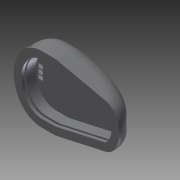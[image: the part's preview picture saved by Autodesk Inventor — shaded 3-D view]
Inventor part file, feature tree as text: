
AUTODESK INVENTOR PART (.ipt)
format: ipt  version: 2015 (Build 190159000, 159)  size: 722,432 bytes
history: native  units: mm
features: extrude x8, sketch x8, fillet x6, projected_geometry x5, plane x1
ambient origin geometry x8: Origin, YZ Plane, XZ Plane, XY Plane, X Axis, Y Axis, Z Axis, Center Point
bodies: Solid1 (feature_tree)
feature tree (28):
  extrude  "Extrusion1"  Depth=60.0mm
  fillet  "Fillet1"  Radius=20.0mm
  extrude  "Extrusion2"  Depth=30.0mm TaperAngle=0.0deg
  fillet  "Fillet6"  Radius=15.0mm
  fillet  "Fillet7"  Radius=110.0mm
  extrude  "Extrusion6"  Depth=60.0mm
  extrude  "Extrusion7"  Depth=5.0mm
  plane  "Work Plane2"
  extrude  "Extrusion8"  Depth=16.0mm
  fillet  "Fillet8"  Radius=8.0mm
  fillet  "Fillet9"  Radius=15.0mm
  extrude  "Extrusion9"  Depth=20.0mm
  extrude  "Extrusion10"  Depth=5.0mm TaperAngle=0.0deg
  fillet  "Fillet10"  Radius=15.5mm
  extrude  "Extrusion12"  Depth=1.0mm
  sketch  "Sketch1"  dims[d0=80.0mm d1=60.0mm d2=20.0mm]
  sketch  "Sketch2"  dims[d3=20.0mm d4=30.0mm d5=0.0mm d6=15.0mm d9=110.0mm]
  sketch  "Sketch6"  dims[d12=50.0mm d13=60.0mm]
  projected_geometry  "Projected Loop3"
  sketch  "Sketch8"  dims[d14=69.25mm d15=0.0mm d33=5.0mm]
  sketch  "Sketch9"  dims[d34=27.0mm d35=16.0mm d36=8.0mm d37=15.0mm d38=0.0mm]
  projected_geometry  "Projected Loop4"
  sketch  "Sketch10"  dims[d40=15.0mm d41=20.0mm]
  projected_geometry  "Projected Loop5"
  sketch  "Sketch11"  dims[d42=8.0mm d43=5.0mm d44=0.0mm d49=15.5mm d50=0.0mm]
  projected_geometry  "Projected Loop6"
  sketch  "Sketch13"  dims[d51=4.0mm d52=1.0mm d53=4.0mm d54=1.0mm d55=4.0mm d56=4.0mm d57=1.0mm d58=2.0mm d60=5.0mm d61=0.0mm d62=8.0mm d63=3.0mm d64=0.0mm d65=20.0mm d66=4.0mm d70=4.0mm d71=3.0mm d72=0.0mm]
  projected_geometry  "Projected Loop8"
